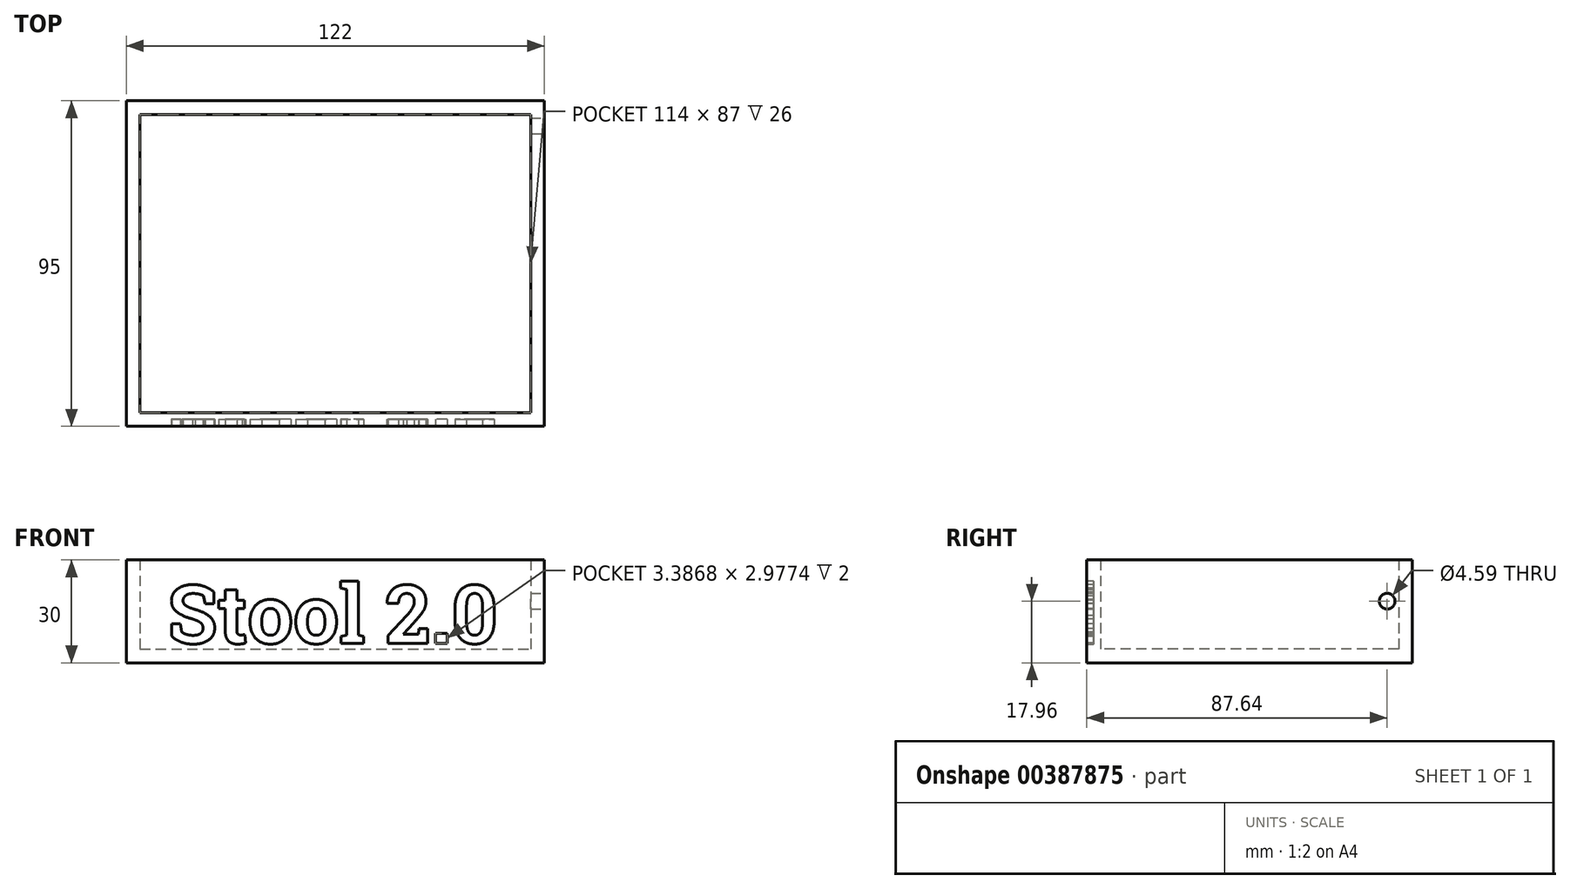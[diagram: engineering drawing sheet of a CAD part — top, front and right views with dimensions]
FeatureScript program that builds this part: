
annotation { "Feature Type Name" : "Feature", "Feature Type Description" : "" }
export const myFeature = defineFeature(function(context is Context, id is Id, definition is map)
    precondition{}
    {
        {
            var Q0;
            Q0=qCreatedBy(makeId("Top.planeOp"),FACE);
            var sketch = newSketch(context, id + "F0", { "sketchPlane" : qUnion([Q0])});
            skLineSegment(sketch, "E0.bottom", {"start": v(-75.95, 57.27) * mm, "end": v(46.05, 57.27) * mm});
            skLineSegment(sketch, "E0.top", {"start": v(-75.95, -37.73) * mm, "end": v(46.05, -37.73) * mm});
            skLineSegment(sketch, "E0.left", {"start": v(-75.95, 57.27) * mm, "end": v(-75.95, -37.73) * mm});
            skLineSegment(sketch, "E0.right", {"start": v(46.05, 57.27) * mm, "end": v(46.05, -37.73) * mm});
            skSolve(sketch);
        }
        {
            var Q0;
            Q0=makeQuery(id+"F0.imprint","IMPRINT",FACE,{"disambiguationData":[TD([[makeQuery(id+"F0.imprint","IMPRINT",EDGE,{"derivedFrom":sQuery(id+"F0.wireOp",EDGE,"E0.bottom")}),-1.0]])]});
            extrude(context, id + "F1", {"entities" : qUnion([Q0]), "depth" : 30 * mm});
        }
        {
            var Q0;
            Q0=makeQuery(id+"F1.opExtrude","CAP_FACE",FACE,{"disambiguationData":[OSD([sQuery(id+"F0.wireOp",EDGE,"E0.bottom"),sQuery(id+"F0.wireOp",EDGE,"E0.top"),sQuery(id+"F0.wireOp",EDGE,"E0.left"),sQuery(id+"F0.wireOp",EDGE,"E0.right")])],"isStart":false});
            shell(context, id + "F2", {"entities" : qUnion([Q0]), "thickness" : 4 * mm});
        }
        {
            var Q0;
            Q0=makeQuery(id+"F1.opExtrude","SWEPT_FACE",FACE,{"disambiguationData":[OSD([sQuery(id+"F0.wireOp",EDGE,"E0.right")])]});
            var sketch = newSketch(context, id + "F3", { "sketchPlane" : qUnion([Q0])});
            skLineSegment(sketch, "E1", {"start": v(-37.73, 15) * mm, "end": v(57.27, 15) * mm});
            skLineSegment(sketch, "E2", {"start": v(57.27, 15) * mm, "end": v(49.9, 17.96) * mm});
            skLineSegment(sketch, "E3", {"start": v(49.9, 17.96) * mm, "end": v(42.95, 15) * mm});
            skSolve(sketch);
        }
        {
            var Q0;
            Q0=sQuery(id+"F3.wireOp",VERTEX,"E3.start");
            var Q1;
            Q1=makeQuery(id+"F1.opExtrude","SWEPT_BODY",BODY,{"disambiguationData":[OSD([sQuery(id+"F0.wireOp",EDGE,"E0.bottom"),sQuery(id+"F0.wireOp",EDGE,"E0.top"),sQuery(id+"F0.wireOp",EDGE,"E0.left"),sQuery(id+"F0.wireOp",EDGE,"E0.right")])]});
            hole(context, id + "F4", {"style" : HoleStyle.SIMPLE, "endStyle" : HoleEndStyle.BLIND, "holeDiameter" : 4.6 * mm, "holeDepth" : 12 * mm, "isTappedThrough" : true, "tappedDepth" : 12 * mm, "tapClearance" : 3, "locations" : qUnion([Q0]), "scope" : qUnion([Q1])});
        }
        {
            var Q0;
            Q0=makeQuery(id+"F1.opExtrude","SWEPT_FACE",FACE,{"disambiguationData":[OSD([sQuery(id+"F0.wireOp",EDGE,"E0.top")])]});
            var sketch = newSketch(context, id + "F5", { "sketchPlane" : qUnion([Q0])});
            skText(sketch, "E4", { "text": "Stool 2.0", "fontName": "RobotoSlab-Bold.ttf"});
            const initialGuessF5  = {"E4": [-0.0639, 0.00567, 1, 0, 0.01715]};
            skSetInitialGuess(sketch, initialGuessF5);
            skSolve(sketch);
        }
        {
            var Q0;
            Q0=makeQuery(id+"F5.imprint","IMPRINT",FACE,{"disambiguationData":[TD([[makeQuery(id+"F5.imprint","IMPRINT",EDGE,{"derivedFrom":sQuery(id+"F5.wireOp",EDGE,"E4.sketch_text.stroke-0")}),-1.0]])]});
            var Q1;
            Q1=makeQuery(id+"F5.imprint","IMPRINT",FACE,{"disambiguationData":[TD([[makeQuery(id+"F5.imprint","IMPRINT",EDGE,{"derivedFrom":sQuery(id+"F5.wireOp",EDGE,"E4.sketch_text.stroke-30")}),-1.0]])]});
            var Q2;
            Q2=makeQuery(id+"F5.imprint","IMPRINT",FACE,{"disambiguationData":[TD([[makeQuery(id+"F5.imprint","IMPRINT",EDGE,{"derivedFrom":sQuery(id+"F5.wireOp",EDGE,"E4.sketch_text.stroke-50")}),-1.0]])]});
            var Q3;
            Q3=makeQuery(id+"F5.imprint","IMPRINT",FACE,{"disambiguationData":[TD([[makeQuery(id+"F5.imprint","IMPRINT",EDGE,{"derivedFrom":sQuery(id+"F5.wireOp",EDGE,"E4.sketch_text.stroke-70")}),-1.0]])]});
            var Q4;
            Q4=makeQuery(id+"F5.imprint","IMPRINT",FACE,{"disambiguationData":[TD([[makeQuery(id+"F5.imprint","IMPRINT",EDGE,{"derivedFrom":sQuery(id+"F5.wireOp",EDGE,"E4.sketch_text.stroke-90")}),-1.0]])]});
            var Q5;
            Q5=makeQuery(id+"F5.imprint","IMPRINT",FACE,{"disambiguationData":[TD([[makeQuery(id+"F5.imprint","IMPRINT",EDGE,{"derivedFrom":sQuery(id+"F5.wireOp",EDGE,"E4.sketch_text.stroke-100")}),-1.0]])]});
            var Q6;
            Q6=makeQuery(id+"F5.imprint","IMPRINT",FACE,{"disambiguationData":[TD([[makeQuery(id+"F5.imprint","IMPRINT",EDGE,{"derivedFrom":sQuery(id+"F5.wireOp",EDGE,"E4.sketch_text.stroke-123")}),-1.0]])]});
            var Q7;
            Q7=makeQuery(id+"F5.imprint","IMPRINT",FACE,{"disambiguationData":[TD([[makeQuery(id+"F5.imprint","IMPRINT",EDGE,{"derivedFrom":sQuery(id+"F5.wireOp",EDGE,"E4.sketch_text.stroke-127")}),-1.0]])]});
            extrude(context, id + "F6", {"entities" : qUnion([Q0, Q1, Q2, Q3, Q4, Q5, Q6, Q7]), "operationType" : NewBodyOperationType.REMOVE, "oppositeDirection" : true, "depth" : 2 * mm});
        }
    });
